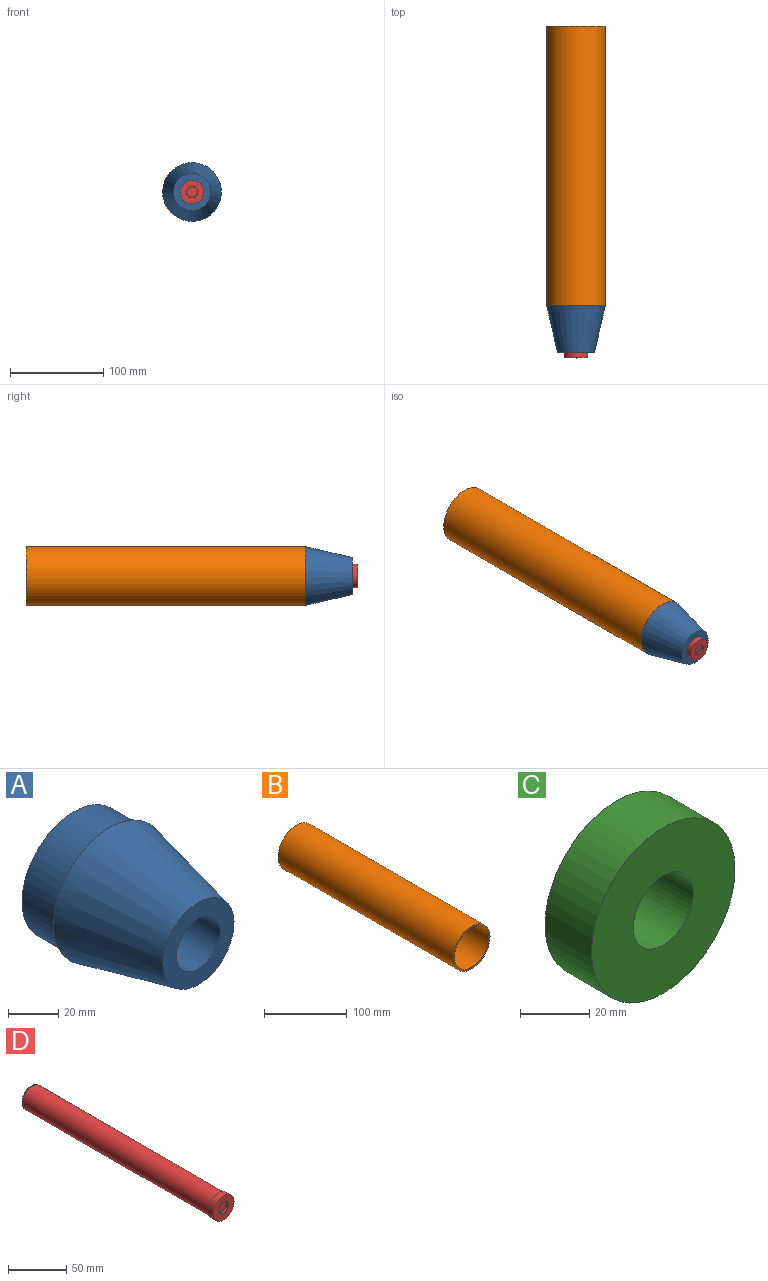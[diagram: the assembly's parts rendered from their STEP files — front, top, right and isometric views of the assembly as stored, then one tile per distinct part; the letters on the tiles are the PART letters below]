
ASSEMBLY  parts=4 mates=5
PART A: 6 faces, bbox 63x70x63 mm
  f0: plane 40x40mm, normal (0,-1,0), area 785.2mm2, adj f2,f5
  f1: plane 63x63mm, normal (0,1,0), area 429.4mm2, adj f2,f3
  f2: cone r=20mm half-angle=13deg, axis (0,1,0), area 8300.8mm2, adj f0,f1
  f3: cylinder r=29.25mm len=58.5mm, axis (0,-1,0), area 3675.7mm2, adj f1,f4
  f4: plane 58.5x58.5mm, normal (0,1,0), area 2216.4mm2, adj f3,f5
  f5: cylinder r=12.25mm len=70mm, axis (0,-1,0), area 5387.8mm2, adj f0,f4
PART B: 4 faces, bbox 63x300x63 mm
  f0: cylinder r=31.5mm len=300mm, axis (0,1,0), area 59376.1mm2, adj f1,f2
  f1: plane 63x63mm, normal (0,-1,0), area 429.4mm2, adj f0,f3
  f2: plane 63x63mm, normal (0,1,0), area 429.4mm2, adj f0,f3
  f3: cylinder r=29.25mm len=300mm, axis (0,-1,0), area 55135mm2, adj f1,f2
PART C: 4 faces, bbox 58.5x19x58.5 mm
  f0: cylinder r=29.25mm len=58.5mm, axis (0,1,0), area 3491.9mm2, adj f1,f2
  f1: plane 58.5x58.5mm, normal (0,-1,0), area 2216.4mm2, adj f0,f3
  f2: plane 58.5x58.5mm, normal (0,1,0), area 2216.4mm2, adj f0,f3
  f3: cylinder r=12.25mm len=24.5mm, axis (0,-1,0), area 1462.4mm2, adj f1,f2
PART D: 8 faces, bbox 25.8x234.4x25.8 mm
  f0: cylinder r=12.7mm len=25.4mm, axis (0,1,0), area 506.7mm2, adj f1,f2
  f1: plane 25.4x25.4mm, normal (0,-1,0), area 393.6mm2, adj f0,f3
  f2: plane 25.4x25.4mm, normal (0,1,0), area 61.8mm2, adj f0,f5
  f3: cylinder r=6mm len=12mm, axis (0,-1,0), area 113.1mm2, adj f1,f4
  f4: plane 12x12mm, normal (0,-1,0), area 113.1mm2, adj f3
  f5: cylinder r=11.9mm len=226.09mm, axis (0,-1,0), area 16904.7mm2, adj f2,f7
  f6: plane 19.8x19.8mm, normal (0,1,0), area 307.9mm2, adj f7
  f7: torus R=9.9mm, axis (0,1,0), area 220.6mm2, adj f5,f6
PLACE A rot(axis=(0,-1,0),10deg) t=(4.02,-83.4,6.61)mm
PLACE B rot(axis=(0,-1,0),10deg) t=(4.02,216.6,6.61)mm
PLACE C rot(axis=(0,-1,0),10deg) t=(4.02,64.64,6.61)mm
PLACE D rot(axis=(0,-1,0),10deg) t=(4.02,-133.4,6.61)mm
MATE slider A.f5 <-> A.f5  axis (0,-1,0) through (4.02,-133.4,6.61)mm
MATE cylindrical C.f3 <-> D.f5  axis (0,1,0) through (4.02,64.64,6.61)mm
MATE fastened A.f2 <-> D.f5  axis (0,1,0) through (4.02,-108.4,6.61)mm
MATE planar D.f0 <-> A.f2  axis (0,1,0) through (4.02,-133.4,6.61)mm
MATE fastened B.f0 <-> A.f3  axis (0,-1,0) through (4.02,-83.4,6.61)mm
